# Revit family: IS_Tesi_T3568_BIM_IT
name_source: partatom
category: Plumbing Fixtures
revit_build: Autodesk Revit MEP 2016 (Build: 20161004_0715(x64)
units: mm (PartAtom-declared; Revit-internal decimal feet)

## family parameters
Always vertical = No
Cut with Voids When Loaded = No
OmniClass Number = 23.45.05.21.11.11
OmniClass Title = Water Operated Water Closets
Part Type = Normal
Room Calculation Point = No
Round Connector Dimension = Use Diameter
Shared = No
Work Plane-Based = No

## types (1)
- T356801 - TESI CASSETTA C/BATT 4.5/3 BEU
    Accessori = www.idealstandard.it
    AltezzaNominale = 387 mm
    Assembly Code = C1030200
    BIMobject category = Toilet Cisterns
    BOSUseNativeGeometries = 1
    Brand = Ideal Standard
    Brand url = http://www.idealstandard.co.uk
    Caratteristiche = Cassetta completa di batteria double flush (4.5/3 litri). Entrata dal basso.
    CodiceABarre = 8014140430674
    CodiceArticolo = T356801
    Colore = Bianco
    Connessione = Installazione
    CostoDiSostituzione = 0 $
    Description = TESI CASSETTA C/BATT 4.5/3 BEU
    Dimensione = 387 x 307 x 174
    DurataGaranzia = 99
    DurataGaranziaProdotti = 99
    EAN code = https://8014140430674
    Edition number = 1
    Finitura = Bianco
    Forma = Sculpture
    Garanzia = Garanzia Idealstandard
    IFC Classification = Sanitary Terminal
    InformaziniGaranzia = www.idealstandard.it/garanzia.html
    InformazioniGaranzia = www.idealstandard.it/garanzia.html
    Installation instructions = http://www.idealstandard.it
    InstruzioniInstallazione = www.idealstandard.it/prodotti/html
    LarghezzaNominale = 307 mm
    LunghezzaNominale = 174 mm
    Manufacturer name = Ideal Standard
    Material main = Ceramics
    Materiale = Porcellana Vetrificata (Vitreous China)
    Model = T356801
    ModelloDiRiferimento = T356802
    NBS Reference Code = 35-93-87
    NBS Reference Description = Wc Cistern Fittings
    Nome = TESI CASSETTA C/BATT 4.5/3 BEU
    Nominal height = 383
    Nominal width = 308
    NumeroDiModello = T356801
    OmniClass Code = 23-31 19 01
    OmniClass Description = Toilets
    PesoNetto = 11 KG
    Product Guid = ebce3941-4cb7-4991-b1a5-b60f801996c1
    Product SKU = T3568
    Product certification = http://www.idealstandard.it
    Product data url = https://bimobject.com
    Product family = TESI
    Product group = WC cisterns
    Product name = Cisterna TESI alimentaci??n inferior 4,5/3 litros, blanca
    Product url = http://www.idealstandard.es
    QR code = http://bimobject.com
    Spazio = Interno
    Technical description = http://www.idealstandard.it
    Telefono = 800 652 290
    TipoDiDato = Fisso
    URL = www.idealstandard.it
    Uniclass 1.4 Code = L72164
    Uniclass 1.4 Description = WC cisterns
    Uniclass 2.0 Code = PR-35-93-87
    Uniclass 2.0 Description = Wc Cistern Fittings
    Uniclass 2015 Code = Pr_40_20_93_87
    Uniclass 2015 Name = WC cistern fittings
    UnitaDurata = anni
    UnitaDurataGaranzia = anni
    UnitaLineare = millimetri
    UnitaSuperficie = millimetri
    UnitaVolume = litri
    Versione = 1
    Weight Net (Kg) = 11

## geometry (parser evidence)
native form markers: Blend x4, Sweep x1
no freeform markers — native parametric forms only
